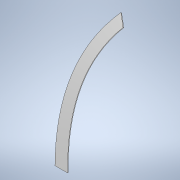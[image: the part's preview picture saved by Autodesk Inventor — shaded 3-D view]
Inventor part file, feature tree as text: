
AUTODESK INVENTOR PART (.ipt)
format: ipt  version: 2021 (Build 250183000, 183)  size: 118,272 bytes
history: native  units: in
note: dims shown in document units (in); Inventor stores cm internally (conversion verified against a paired STEP export)
features: sketch x2, sweep x1
ambient origin geometry x8: Origin, YZ Plane, XZ Plane, XY Plane, X Axis, Y Axis, Z Axis, Center Point
bodies: Solid1 (feature_tree)
feature tree (3):
  sweep  "Sweep1"
  sketch  "Sketch1"  dims[d0=2.0in d1=0.1in d4=0.0in d5=0.0in]
  sketch  "3D Sketch1"
